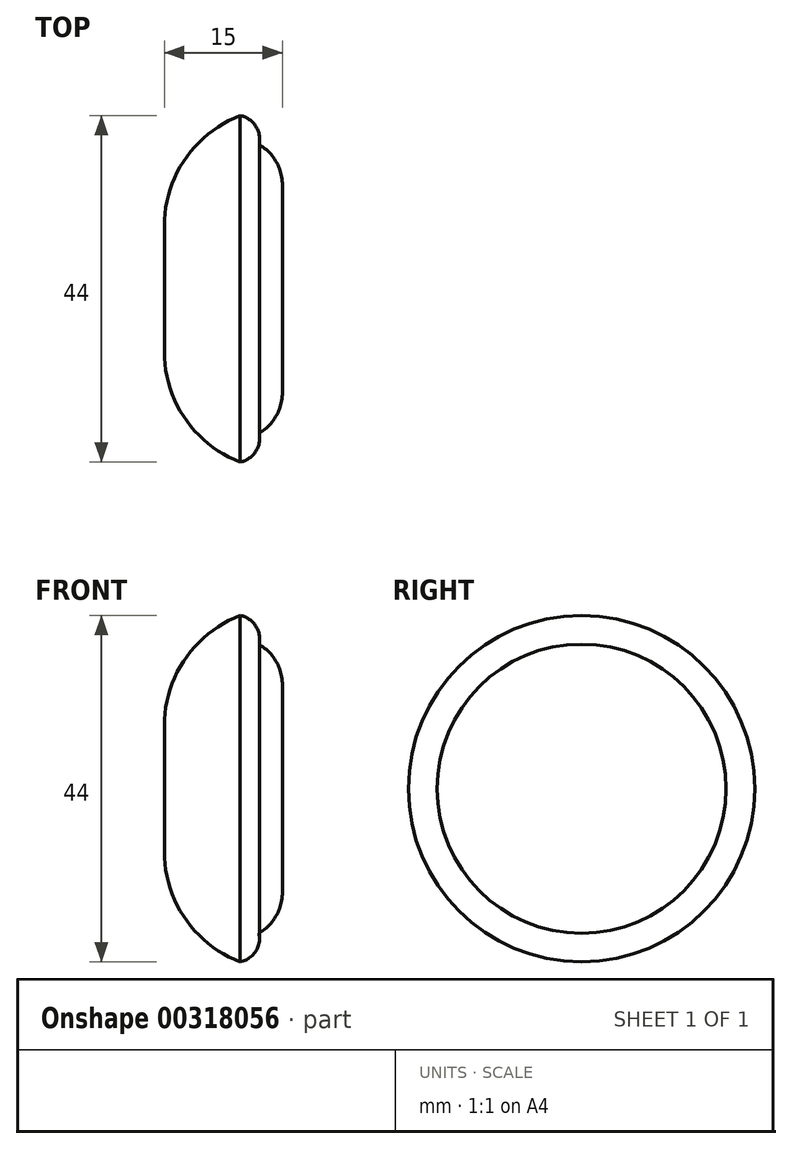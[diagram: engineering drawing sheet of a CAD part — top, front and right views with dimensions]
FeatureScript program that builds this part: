
annotation { "Feature Type Name" : "Feature", "Feature Type Description" : "" }
export const myFeature = defineFeature(function(context is Context, id is Id, definition is map)
    precondition{}
    {
        {
            var Q0;
            Q0=qCreatedBy(makeId("Front.planeOp"),FACE);
            var sketch = newSketch(context, id + "F0", { "sketchPlane" : qUnion([Q0])});
            skLineSegment(sketch, "E0", {"start": v(0, 0) * mm, "end": v(0, 8) * mm});
            skArc(sketch, "E1", {"start": v(9.61, 22) * mm, "mid": v(2.64, 16.5) * mm, "end": v(0, 8) * mm});
            skArc(sketch, "E2", {"start": v(12, 18.35) * mm, "mid": v(11.6, 20.69) * mm, "end": v(9.61, 22) * mm});
            skLineSegment(sketch, "E3", {"start": v(12, 18.35) * mm, "end": v(12, 0) * mm, "construction": true});
            skArc(sketch, "E4", {"start": v(15, 13.16) * mm, "mid": v(14.2, 16.16) * mm, "end": v(12, 18.35) * mm});
            skLineSegment(sketch, "E5", {"start": v(15, 13.16) * mm, "end": v(15, 0) * mm});
            skLineSegment(sketch, "E6", {"start": v(15, 0) * mm, "end": v(0, 0) * mm});
            skSolve(sketch);
        }
        {
            var Q0;
            Q0=makeQuery(id+"F0.imprint","IMPRINT",FACE,{"disambiguationData":[TD([[makeQuery(id+"F0.imprint","IMPRINT",EDGE,{"derivedFrom":sQuery(id+"F0.wireOp",EDGE,"E0")}),-1.0]])]});
            var Q1;
            Q1=sQuery(id+"F0.wireOp",EDGE,"E6");
            revolve(context, id + "F1", {"entities" : qUnion([Q0]), "axis" : qUnion([Q1]), "revolveType" : RevolveType.FULL});
        }
    });
